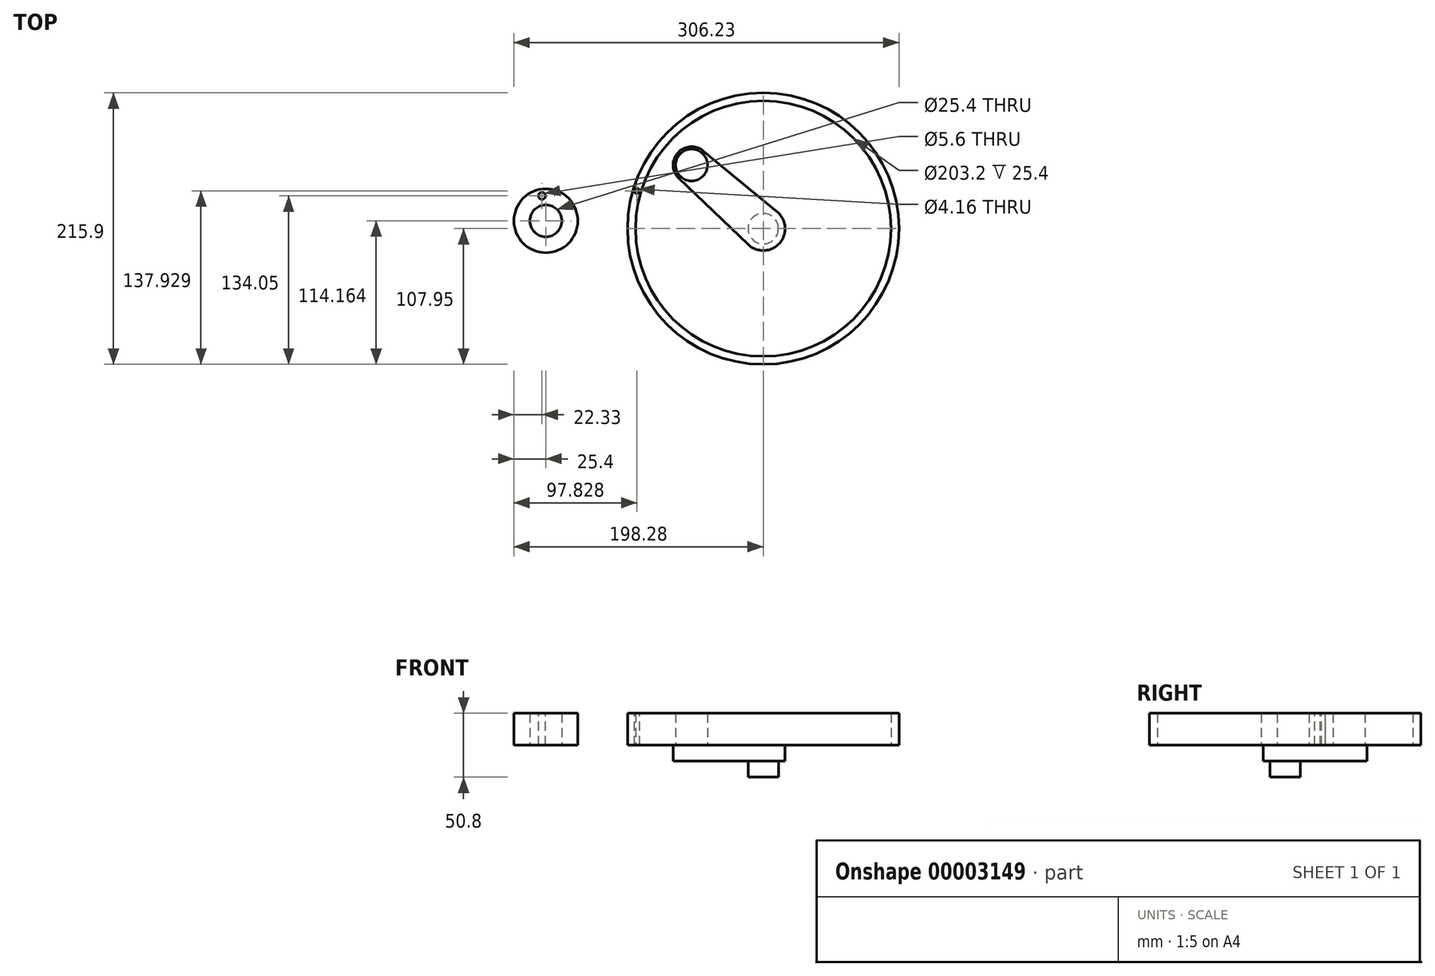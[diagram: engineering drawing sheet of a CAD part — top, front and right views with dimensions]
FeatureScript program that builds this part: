
annotation { "Feature Type Name" : "Feature", "Feature Type Description" : "" }
export const myFeature = defineFeature(function(context is Context, id is Id, definition is map)
    precondition{}
    {
        {
            var Q0;
            Q0=qCreatedBy(makeId("Top.planeOp"),FACE);
            var sketch = newSketch(context, id + "F0", { "sketchPlane" : qUnion([Q0])});
            skCircle(sketch, "E0", {"center": v(0, 0) * mm, "radius": 107.95 * mm});
            skCircle(sketch, "E1", {"center": v(0, 0) * mm, "radius": 101.6 * mm});
            skSolve(sketch);
        }
        {
            var Q0;
            Q0=makeQuery(id+"F0.imprint","IMPRINT",FACE,{"disambiguationData":[TD([[makeQuery(id+"F0.imprint","IMPRINT",EDGE,{"derivedFrom":sQuery(id+"F0.wireOp",EDGE,"E0")}),1.0]])]});
            extrude(context, id + "F1", {"entities" : qUnion([Q0]), "depth" : 25.4 * mm});
        }
        {
            var Q0;
            Q0=qCreatedBy(makeId("Top.planeOp"),FACE);
            var sketch = newSketch(context, id + "F2", { "sketchPlane" : qUnion([Q0])});
            skCircle(sketch, "E2", {"center": v(-57, 50.57) * mm, "radius": 12.7 * mm});
            skCircle(sketch, "E3", {"center": v(0, 0) * mm, "radius": 17.41 * mm});
            skCircle(sketch, "E4", {"center": v(-57, 50.57) * mm, "radius": 14.61 * mm});
            skCircle(sketch, "E5", {"center": v(0, 0) * mm, "radius": 12.06 * mm});
            skLineSegment(sketch, "E6", {"start": v(-47.71, 61.85) * mm, "end": v(11.07, 13.44) * mm});
            skLineSegment(sketch, "E7", {"start": v(-67.1, 40) * mm, "end": v(-12.03, -12.6) * mm});
            skSolve(sketch);
        }
        {
            var Q0;
            {var subQ3=sQuery(id+"F2.wireOp",EDGE,"E6");Q0=qUnion([makeQuery(id+"F2.imprint","IMPRINT",FACE,{"disambiguationData":[TD([[makeQuery(id+"F2.imprint","IMPRINT",EDGE,{"derivedFrom":sQuery(id+"F2.wireOp",EDGE,"E2")}),-1.0]])]}),makeQuery(id+"F2.imprint","IMPRINT",FACE,{"disambiguationData":[TD([[makeQuery(id+"F2.imprint","IMPRINT",EDGE,{"derivedFrom":sQuery(id+"F2.wireOp",EDGE,"E5")}),-1.0]])]}),makeQuery(id+"F2.imprint","IMPRINT",FACE,{"disambiguationData":[TD([[makeQuery(id+"F2.imprint","IMPRINT",EDGE,{"derivedFrom":subQ3}),-1.0]])]})]);}
            var Q1;
            Q1=makeQuery(id+"F2.imprint","IMPRINT",FACE,{"disambiguationData":[TD([[makeQuery(id+"F2.imprint","IMPRINT",EDGE,{"derivedFrom":sQuery(id+"F2.wireOp",EDGE,"E2")}),1.0]])]});
            var Q2;
            Q2=makeQuery(id+"F2.imprint","IMPRINT",FACE,{"disambiguationData":[TD([[makeQuery(id+"F2.imprint","IMPRINT",EDGE,{"derivedFrom":sQuery(id+"F2.wireOp",EDGE,"E5")}),1.0]])]});
            extrude(context, id + "F3", {"entities" : qUnion([Q0, Q1, Q2]), "oppositeDirection" : true, "depth" : 12.7 * mm});
        }
        {
            var Q0;
            Q0=makeQuery(id+"F2.imprint","IMPRINT",FACE,{"disambiguationData":[TD([[makeQuery(id+"F2.imprint","IMPRINT",EDGE,{"derivedFrom":sQuery(id+"F2.wireOp",EDGE,"E2")}),1.0]])]});
            extrude(context, id + "F4", {"entities" : qUnion([Q0]), "operationType" : NewBodyOperationType.ADD, "depth" : 25.4 * mm});
        }
        {
            var Q0;
            Q0=makeQuery(id+"F2.imprint","IMPRINT",FACE,{"disambiguationData":[TD([[makeQuery(id+"F2.imprint","IMPRINT",EDGE,{"derivedFrom":sQuery(id+"F2.wireOp",EDGE,"E5")}),1.0]])]});
            var Q1;
            Q1=sQuery(id+"F2.wireOp",EDGE,"E5");
            extrude(context, id + "F5", {"entities" : qUnion([Q0]), "operationType" : NewBodyOperationType.ADD, "surfaceEntities" : qUnion([Q1]), "oppositeDirection" : true, "depth" : 25.4 * mm});
        }
        {
            var Q0;
            Q0=qCreatedBy(makeId("Top.planeOp"),FACE);
            var sketch = newSketch(context, id + "F6", { "sketchPlane" : qUnion([Q0])});
            skCircle(sketch, "E8", {"center": v(-172.88, 6.21) * mm, "radius": 25.4 * mm});
            skCircle(sketch, "E9", {"center": v(-172.88, 6.21) * mm, "radius": 12.7 * mm});
            skSolve(sketch);
        }
        {
            var Q0;
            Q0=makeQuery(id+"F6.imprint","IMPRINT",FACE,{"disambiguationData":[TD([[makeQuery(id+"F6.imprint","IMPRINT",EDGE,{"derivedFrom":sQuery(id+"F6.wireOp",EDGE,"E8")}),1.0]])]});
            extrude(context, id + "F7", {"entities" : qUnion([Q0]), "depth" : 25.4 * mm});
        }
        {
            var Q0;
            Q0=makeQuery(id+"F7.opExtrude","CAP_FACE",FACE,{"disambiguationData":[OSD([sQuery(id+"F6.wireOp",EDGE,"E8"),sQuery(id+"F6.wireOp",EDGE,"E9")])],"isStart":false});
            var sketch = newSketch(context, id + "F8", { "sketchPlane" : qUnion([Q0])});
            skCircle(sketch, "E10", {"center": v(-175.95, 26.1) * mm, "radius": 2.8 * mm});
            skSolve(sketch);
        }
        {
            var Q0;
            Q0=makeQuery(id+"F8.imprint","IMPRINT",FACE,{"disambiguationData":[TD([[makeQuery(id+"F8.imprint","IMPRINT",EDGE,{"derivedFrom":sQuery(id+"F8.wireOp",EDGE,"E10")}),1.0]])]});
            extrude(context, id + "F9", {"entities" : qUnion([Q0]), "operationType" : NewBodyOperationType.REMOVE, "endBound" : BoundingType.THROUGH_ALL, "oppositeDirection" : true, "depth" : 25.4 * mm});
        }
        {
            var Q0;
            Q0=makeQuery(id+"F1.opExtrude","CAP_FACE",FACE,{"disambiguationData":[OSD([sQuery(id+"F0.wireOp",EDGE,"E0"),sQuery(id+"F0.wireOp",EDGE,"E1")])],"isStart":false});
            var sketch = newSketch(context, id + "F10", { "sketchPlane" : qUnion([Q0])});
            skCircle(sketch, "E11", {"center": v(-100.45, 29.98) * mm, "radius": 2.08 * mm});
            skSolve(sketch);
        }
        {
            var Q0;
            Q0=makeQuery(id+"F10.imprint","IMPRINT",FACE,{"disambiguationData":[TD([[makeQuery(id+"F10.imprint","IMPRINT",EDGE,{"derivedFrom":sQuery(id+"F10.wireOp",EDGE,"E11")}),1.0]])]});
            extrude(context, id + "F11", {"entities" : qUnion([Q0]), "operationType" : NewBodyOperationType.REMOVE, "endBound" : BoundingType.THROUGH_ALL, "oppositeDirection" : true, "depth" : 25.4 * mm});
        }
    });
